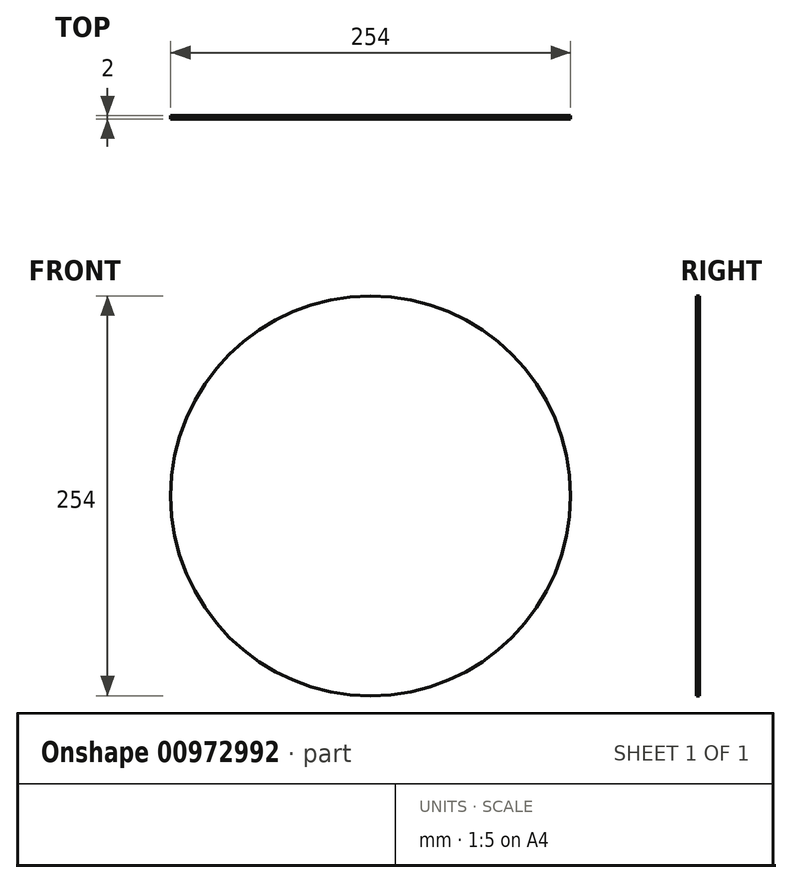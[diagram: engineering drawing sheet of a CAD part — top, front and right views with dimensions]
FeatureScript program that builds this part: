
annotation { "Feature Type Name" : "Feature", "Feature Type Description" : "" }
export const myFeature = defineFeature(function(context is Context, id is Id, definition is map)
    precondition{}
    {
        {
            var Q0;
            Q0=qCreatedBy(makeId("Front.planeOp"),FACE);
            var sketch = newSketch(context, id + "F0", { "sketchPlane" : qUnion([Q0])});
            skCircle(sketch, "E0", {"center": v(0, 0) * mm, "radius": 127 * mm});
            skSolve(sketch);
        }
        {
            var Q0;
            Q0 = qSketchRegion(id + "F0", true);
            extrude(context, id + "F1", {"entities" : qUnion([Q0]), "depth" : 2 * mm, "offsetDistance" : 25 * mm});
        }
    });
